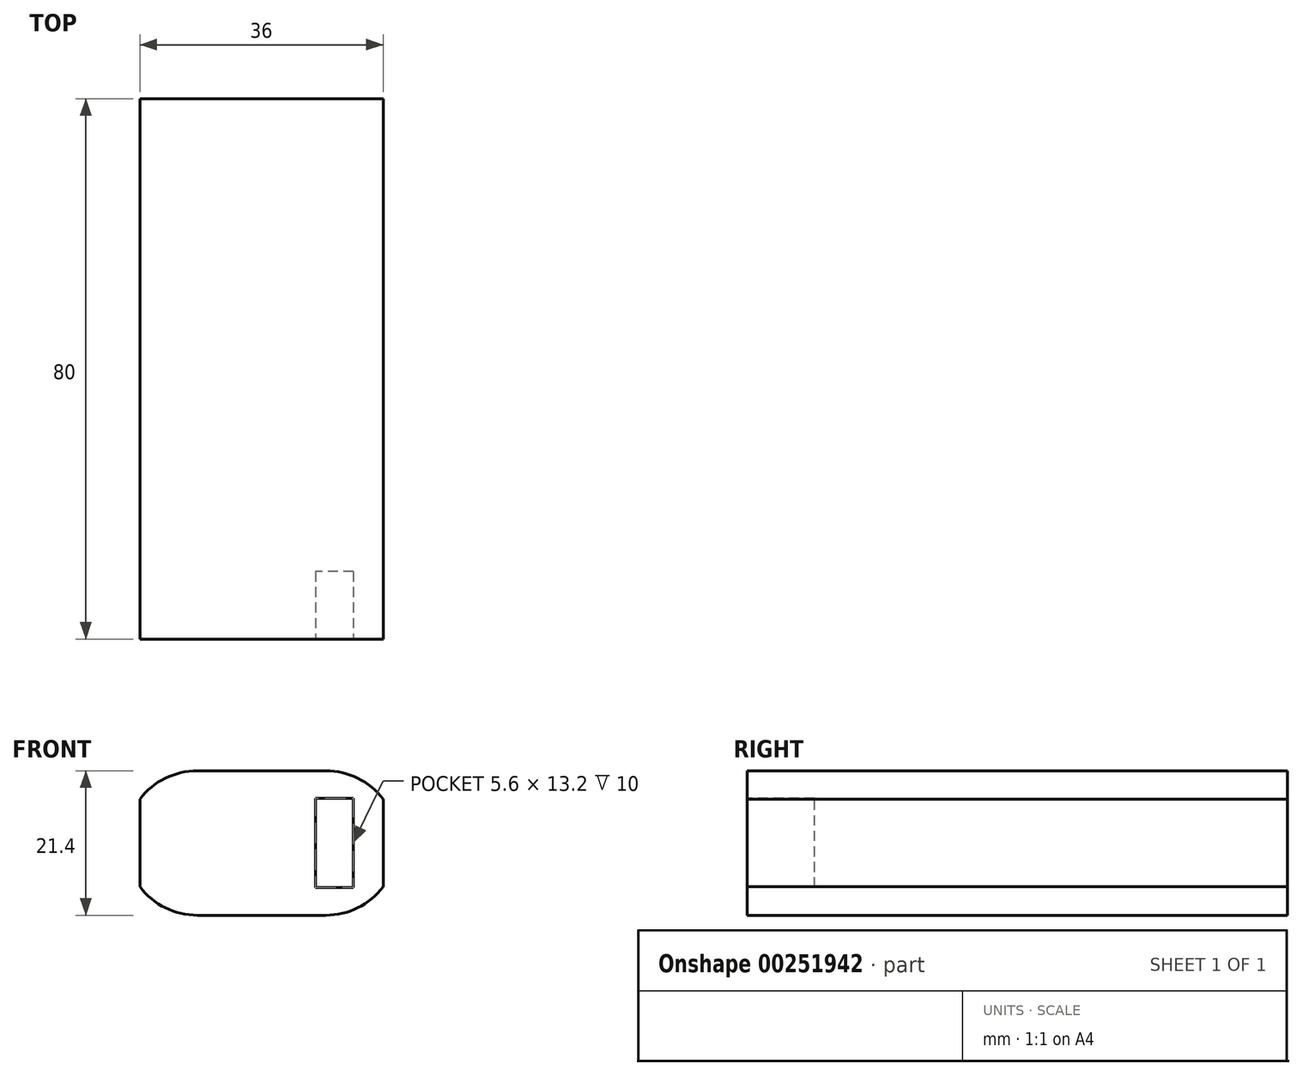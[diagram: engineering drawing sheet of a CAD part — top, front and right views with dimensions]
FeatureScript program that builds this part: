
annotation { "Feature Type Name" : "Feature", "Feature Type Description" : "" }
export const myFeature = defineFeature(function(context is Context, id is Id, definition is map)
    precondition{}
    {
        {
            var Q0;
            Q0=qCreatedBy(makeId("Front.planeOp"),FACE);
            var sketch = newSketch(context, id + "F0", { "sketchPlane" : qUnion([Q0])});
            skLineSegment(sketch, "E0.bottom", {"start": v(9.5, -10.7) * mm, "end": v(-9.5, -10.7) * mm});
            skLineSegment(sketch, "E0.top", {"start": v(9.5, 10.7) * mm, "end": v(-9.5, 10.7) * mm});
            skLineSegment(sketch, "E0.left", {"start": v(18, -6.5) * mm, "end": v(18, 6.5) * mm});
            skLineSegment(sketch, "E0.right", {"start": v(-18, -6.5) * mm, "end": v(-18, 6.5) * mm});
            skPoint(sketch, "E0.middle", {"position": v(0, 0) * mm});
            skLineSegment(sketch, "E1", {"start": v(0, 0) * mm, "end": v(-28.08, 0) * mm, "construction": true});
            skPoint(sketch, "E1.endSnap0", {"position": v(-18, 0) * mm});
            skLineSegment(sketch, "E2", {"start": v(0, 0) * mm, "end": v(0, 17.59) * mm, "construction": true});
            skPoint(sketch, "E2.endSnap0", {"position": v(0, 10.7) * mm});
            skArc(sketch, "E3", {"start": v(-9.5, 10.7) * mm, "mid": v(-14.24, 9.6) * mm, "end": v(-18, 6.5) * mm});
            skArc(sketch, "E4.MirrorCS", {"start": v(9.5, 10.7) * mm, "mid": v(14.24, 9.6) * mm, "end": v(18, 6.5) * mm});
            skArc(sketch, "E5.MirrorCS", {"start": v(-9.5, -10.7) * mm, "mid": v(-14.24, -9.6) * mm, "end": v(-18, -6.5) * mm});
            skArc(sketch, "E6.MirrorCS", {"start": v(9.5, -10.7) * mm, "mid": v(14.24, -9.6) * mm, "end": v(18, -6.5) * mm});
            skPoint(sketch, "E7.orphan", {"position": v(-18, 10.7) * mm});
            skPoint(sketch, "E8.orphan", {"position": v(18, 10.7) * mm});
            skPoint(sketch, "E9.orphan", {"position": v(18, -10.7) * mm});
            skPoint(sketch, "E10.orphan", {"position": v(-18, -10.7) * mm});
            skSolve(sketch);
        }
        {
            var Q0;
            Q0=makeQuery(id+"F0.imprint","IMPRINT",FACE,{"disambiguationData":[TD([[makeQuery(id+"F0.imprint","IMPRINT",EDGE,{"derivedFrom":sQuery(id+"F0.wireOp",EDGE,"E0.bottom")}),-1.0]])]});
            extrude(context, id + "F1", {"entities" : qUnion([Q0]), "endBound" : BoundingType.SYMMETRIC, "depth" : 80 * mm});
        }
        {
            var Q0;
            Q0=makeQuery(id+"F1.opExtrude","CAP_FACE",FACE,{"disambiguationData":[OSD([sQuery(id+"F0.wireOp",EDGE,"E0.bottom"),sQuery(id+"F0.wireOp",EDGE,"E0.top"),sQuery(id+"F0.wireOp",EDGE,"E0.left"),sQuery(id+"F0.wireOp",EDGE,"E0.right"),sQuery(id+"F0.wireOp",EDGE,"E3"),sQuery(id+"F0.wireOp",EDGE,"E4.MirrorCS"),sQuery(id+"F0.wireOp",EDGE,"E5.MirrorCS"),sQuery(id+"F0.wireOp",EDGE,"E6.MirrorCS")])],"isStart":false});
            var sketch = newSketch(context, id + "F2", { "sketchPlane" : qUnion([Q0])});
            skLineSegment(sketch, "E11.bottom", {"start": v(13.6, -6.6) * mm, "end": v(8, -6.6) * mm});
            skLineSegment(sketch, "E11.top", {"start": v(13.6, 6.6) * mm, "end": v(8, 6.6) * mm});
            skLineSegment(sketch, "E11.left", {"start": v(13.6, -6.6) * mm, "end": v(13.6, 6.6) * mm});
            skLineSegment(sketch, "E11.right", {"start": v(8, -6.6) * mm, "end": v(8, 6.6) * mm});
            skPoint(sketch, "E11.middle", {"position": v(10.8, 0) * mm});
            skSolve(sketch);
        }
        {
            var Q0;
            Q0=makeQuery(id+"F2.imprint","IMPRINT",FACE,{"disambiguationData":[TD([[makeQuery(id+"F2.imprint","IMPRINT",EDGE,{"derivedFrom":sQuery(id+"F2.wireOp",EDGE,"E11.bottom")}),-1.0]])]});
            extrude(context, id + "F3", {"entities" : qUnion([Q0]), "operationType" : NewBodyOperationType.REMOVE, "oppositeDirection" : true, "depth" : 10 * mm});
        }
    });
